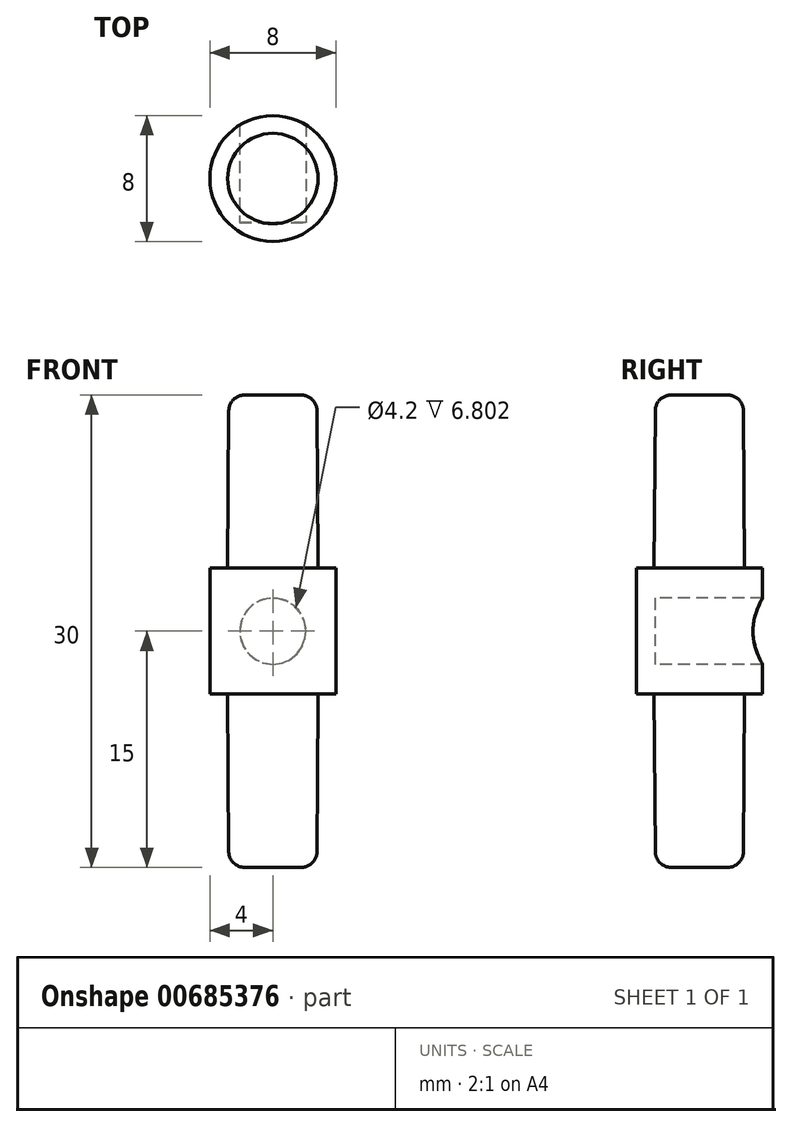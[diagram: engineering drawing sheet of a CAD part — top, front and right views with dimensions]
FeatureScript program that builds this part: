
annotation { "Feature Type Name" : "Feature", "Feature Type Description" : "" }
export const myFeature = defineFeature(function(context is Context, id is Id, definition is map)
    precondition{}
    {
        {
            var Q0;
            Q0=qCreatedBy(makeId("Top.planeOp"),FACE);
            var sketch = newSketch(context, id + "F0", { "sketchPlane" : qUnion([Q0])});
            skCircle(sketch, "E0", {"center": v(0, 0) * mm, "radius": 2.9 * mm});
            skCircle(sketch, "E1", {"center": v(0, 0) * mm, "radius": 4 * mm});
            skSolve(sketch);
        }
        {
            var Q0;
            Q0=makeQuery(id+"F0.imprint","IMPRINT",FACE,{"disambiguationData":[TD([[makeQuery(id+"F0.imprint","IMPRINT",EDGE,{"derivedFrom":sQuery(id+"F0.wireOp",EDGE,"E0")}),1.0]])]});
            extrude(context, id + "F1", {"entities" : qUnion([Q0]), "depth" : 15 * mm, "offsetDistance" : 25 * mm, "hasDraft" : true, "draftAngle" : 0.4 * degree, "draftPullDirection" : true});
        }
        {
            var Q0;
            Q0=makeQuery(id+"F0.imprint","IMPRINT",FACE,{"disambiguationData":[TD([[makeQuery(id+"F0.imprint","IMPRINT",EDGE,{"derivedFrom":sQuery(id+"F0.wireOp",EDGE,"E0")}),1.0]])]});
            extrude(context, id + "F2", {"entities" : qUnion([Q0]), "operationType" : NewBodyOperationType.ADD, "oppositeDirection" : true, "depth" : 15 * mm, "offsetDistance" : 25 * mm, "hasDraft" : true, "draftAngle" : .4 * degree, "draftPullDirection" : true});
        }
        {
            var Q0;
            Q0=makeQuery(id+"F0.imprint","IMPRINT",FACE,{"disambiguationData":[TD([[makeQuery(id+"F0.imprint","IMPRINT",EDGE,{"derivedFrom":sQuery(id+"F0.wireOp",EDGE,"E0")}),-1.0]])]});
            var Q1;
            Q1=makeQuery(id+"F0.imprint","IMPRINT",FACE,{"disambiguationData":[TD([[makeQuery(id+"F0.imprint","IMPRINT",EDGE,{"derivedFrom":sQuery(id+"F0.wireOp",EDGE,"E0")}),1.0]])]});
            extrude(context, id + "F3", {"entities" : qUnion([Q0, Q1]), "operationType" : NewBodyOperationType.ADD, "depth" : 4 * mm, "offsetDistance" : 25 * mm});
        }
        {
            var Q0;
            Q0=makeQuery(id+"F0.imprint","IMPRINT",FACE,{"disambiguationData":[TD([[makeQuery(id+"F0.imprint","IMPRINT",EDGE,{"derivedFrom":sQuery(id+"F0.wireOp",EDGE,"E0")}),-1.0]])]});
            var Q1;
            Q1=makeQuery(id+"F0.imprint","IMPRINT",FACE,{"disambiguationData":[TD([[makeQuery(id+"F0.imprint","IMPRINT",EDGE,{"derivedFrom":sQuery(id+"F0.wireOp",EDGE,"E0")}),1.0]])]});
            extrude(context, id + "F4", {"entities" : qUnion([Q0, Q1]), "operationType" : NewBodyOperationType.ADD, "oppositeDirection" : true, "depth" : 4 * mm, "offsetDistance" : 25 * mm});
        }
        {
            var Q0;
            Q0=makeQuery(id+"F1.opExtrude","CAP_EDGE",EDGE,{"disambiguationData":[OSD([sQuery(id+"F0.wireOp",EDGE,"E0")])],"isStart":false});
            var Q1;
            Q1=makeQuery(id+"F2.opExtrude","CAP_EDGE",EDGE,{"disambiguationData":[OSD([sQuery(id+"F0.wireOp",EDGE,"E0")])],"isStart":false});
            fillet(context, id + "F5", {"entities" : qUnion([Q0, Q1]), "radius" : 1 * mm, "tangentPropagation" : true, "allowEdgeOverflow" : false});
        }
        {
            var Q0;
            Q0=qCreatedBy(makeId("Front.planeOp"),FACE);
            var sketch = newSketch(context, id + "F6", { "sketchPlane" : qUnion([Q0])});
            skCircle(sketch, "E2", {"center": v(0, 0) * mm, "radius": 2.1 * mm});
            skSolve(sketch);
        }
        {
            var Q0;
            Q0=makeQuery(id+"F6.imprint","IMPRINT",FACE,{"disambiguationData":[TD([[makeQuery(id+"F6.imprint","IMPRINT",EDGE,{"derivedFrom":sQuery(id+"F6.wireOp",EDGE,"E2")}),1.0]])]});
            extrude(context, id + "F7", {"entities" : qUnion([Q0]), "operationType" : NewBodyOperationType.REMOVE, "oppositeDirection" : true, "depth" : 4.2 * mm, "offsetDistance" : 25 * mm});
        }
        {
            var Q0;
            Q0=makeQuery(id+"F6.imprint","IMPRINT",FACE,{"disambiguationData":[TD([[makeQuery(id+"F6.imprint","IMPRINT",EDGE,{"derivedFrom":sQuery(id+"F6.wireOp",EDGE,"E2")}),1.0]])]});
            extrude(context, id + "F8", {"entities" : qUnion([Q0]), "operationType" : NewBodyOperationType.REMOVE, "depth" : 2.8 * mm, "offsetDistance" : 25 * mm});
        }
    });
